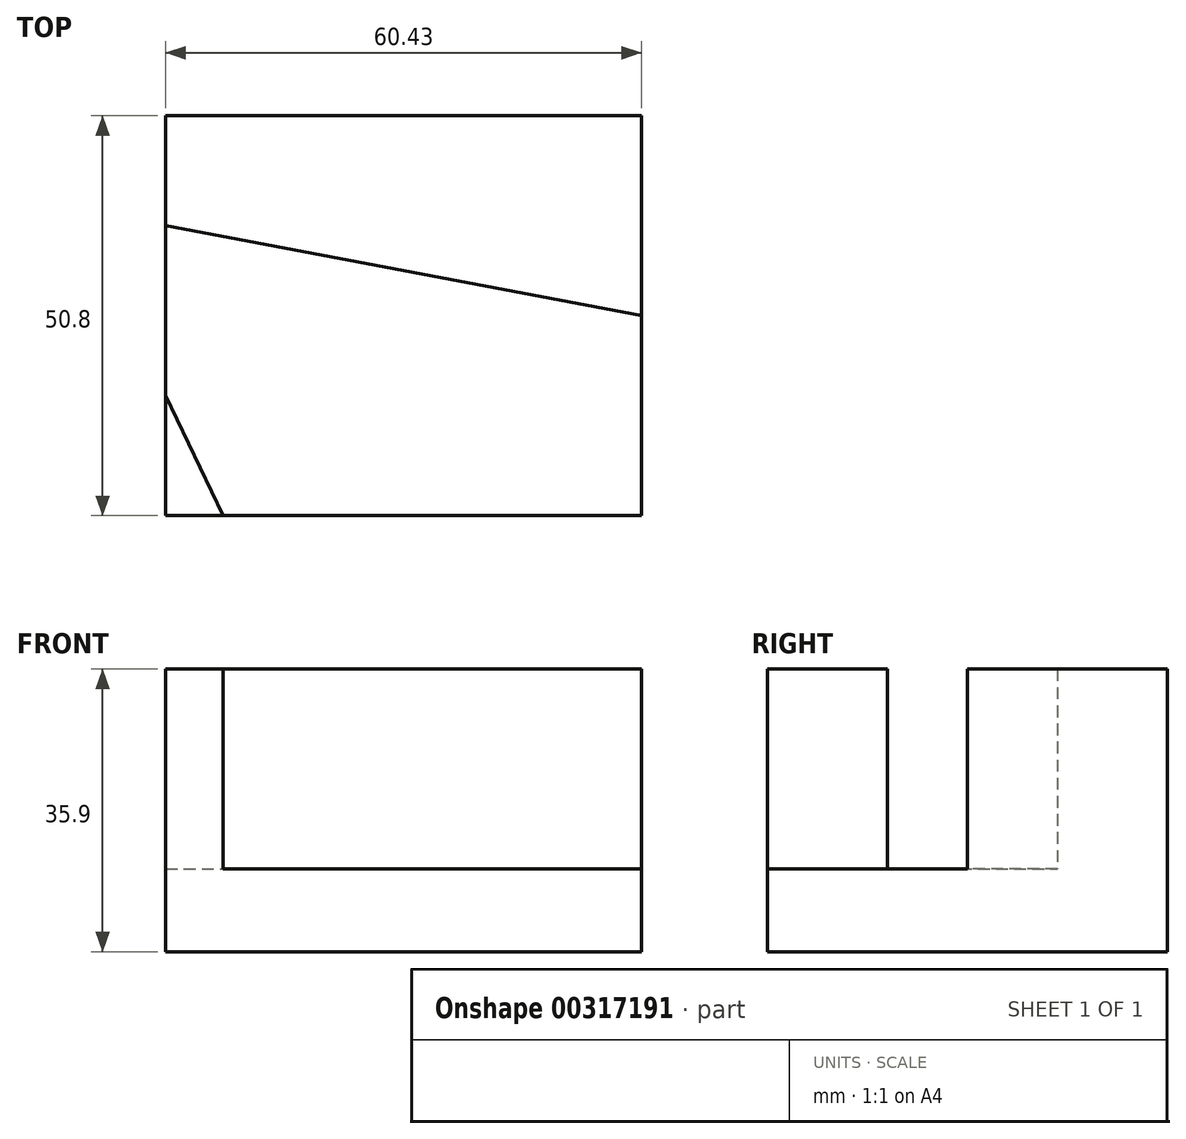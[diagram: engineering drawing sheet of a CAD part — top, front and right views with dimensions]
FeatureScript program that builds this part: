
annotation { "Feature Type Name" : "Feature", "Feature Type Description" : "" }
export const myFeature = defineFeature(function(context is Context, id is Id, definition is map)
    precondition{}
    {
        {
            var Q0;
            Q0=qCreatedBy(makeId("Front.planeOp"),FACE);
            var sketch = newSketch(context, id + "F0", { "sketchPlane" : qUnion([Q0])});
            skLineSegment(sketch, "E0", {"start": v(-50.36, -16.17) * mm, "end": v(10.07, -16.17) * mm});
            skLineSegment(sketch, "E1", {"start": v(10.07, -16.17) * mm, "end": v(10.07, -5.67) * mm});
            skLineSegment(sketch, "E2", {"start": v(10.07, -5.67) * mm, "end": v(-50.36, -5.67) * mm});
            skLineSegment(sketch, "E3", {"start": v(-50.36, -5.67) * mm, "end": v(-50.36, -16.17) * mm});
            skSolve(sketch);
        }
        {
            var Q0;
            Q0=makeQuery(id+"F0.imprint","IMPRINT",FACE,{"disambiguationData":[TD([[makeQuery(id+"F0.imprint","IMPRINT",EDGE,{"derivedFrom":sQuery(id+"F0.wireOp",EDGE,"E0")}),1.0]])]});
            extrude(context, id + "F1", {"entities" : qUnion([Q0]), "depth" : 50.8 * mm});
        }
        {
            var Q0;
            Q0=makeQuery(id+"F1.opExtrude","SWEPT_FACE",FACE,{"disambiguationData":[OSD([sQuery(id+"F0.wireOp",EDGE,"E2")])]});
            var sketch = newSketch(context, id + "F2", { "sketchPlane" : qUnion([Q0])});
            skLineSegment(sketch, "E4", {"start": v(-50.36, -35.54) * mm, "end": v(-43.04, -50.8) * mm});
            skLineSegment(sketch, "E5", {"start": v(-43.04, -50.8) * mm, "end": v(-50.36, -50.8) * mm});
            skLineSegment(sketch, "E6", {"start": v(-50.36, -50.8) * mm, "end": v(-50.36, -35.54) * mm});
            skLineSegment(sketch, "E7", {"start": v(-50.36, -13.97) * mm, "end": v(10.07, -25.4) * mm});
            skLineSegment(sketch, "E8", {"start": v(10.07, -25.4) * mm, "end": v(10.07, 0) * mm});
            skLineSegment(sketch, "E9", {"start": v(10.07, 0) * mm, "end": v(-50.36, 0) * mm});
            skLineSegment(sketch, "E10", {"start": v(-50.36, 0) * mm, "end": v(-50.36, -13.97) * mm});
            skSolve(sketch);
        }
        {
            var Q0;
            Q0=makeQuery(id+"F2.imprint","IMPRINT",FACE,{"disambiguationData":[TD([[makeQuery(id+"F2.imprint","IMPRINT",EDGE,{"derivedFrom":sQuery(id+"F2.wireOp",EDGE,"E4")}),-1.0]])]});
            var Q1;
            Q1=makeQuery(id+"F2.imprint","IMPRINT",FACE,{"disambiguationData":[TD([[makeQuery(id+"F2.imprint","IMPRINT",EDGE,{"derivedFrom":sQuery(id+"F2.wireOp",EDGE,"E7")}),1.0]])]});
            extrude(context, id + "F3", {"entities" : qUnion([Q0, Q1]), "operationType" : NewBodyOperationType.ADD, "depth" : 25.4 * mm});
        }
    });
